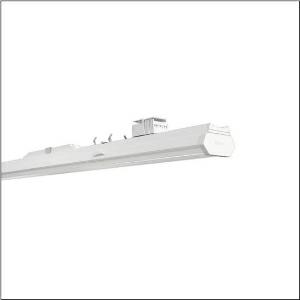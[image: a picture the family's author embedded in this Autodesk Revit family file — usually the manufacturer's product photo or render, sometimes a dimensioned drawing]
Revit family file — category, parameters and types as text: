
# Revit family: licross_r__11_protected_mo_51ts12cn475fd_3ab4
name_source: partatom
category: Lighting Fixtures
units: mm (PartAtom-declared; Revit-internal decimal feet)

## family parameters
Cut with Voids When Loaded = No
Host = Face
Light Source = No
Part Type = Normal
Room Calculation Point = No
Round Connector Dimension = Use Diameter
Shared = No

## types (1)
- --- (1 x LED, 3110 lm, 17.7 W, 4000K)
    Apparent Load = 18 VA
    CIE Flux Codes = 54 82 95 97 100
    Color Rendering = 80
    Color Temperature = 4000K
    Default Elevation = 1800 mm
    Description = Licross® 11 Protected MOluminaire insert, length: 1.500mm, width: 90mm, height: 101mm, LED rated luminous flux: 7.680lm, light colour: 840, control gear: ON/OFF Multilumen, CLOi, control gear: ECG Multilumen, with plug, 6-pole, with phase selection, mains connection: 220..240V, AC/DC, 0/50..60Hz, without changeover relay, for emergency light function, for central battery installations according to DIN EN 60598-2-22, halogen-free wiring, primary optical cover: cover, of PMMA, light emission: direct with ceiling illumination distribution, protection rating (complete): IP50, insulation class (complete): insulation class I (protective earthing), certification: CE, ENEC, VDE, protection symbol: D if used in an environment without relevant dust loads with corresponding accessories, permissible ambient temperature for indoor applications: -35..+40°C, standard: EN 60598-2-22, reducing of maximum allowable ambient temperature of 5°C with ceiling mounting, corresponds to IFS (International Featured Standards) requirements for safety and quality in the food industry, packaging unit: 1 piece
    Height = 92 mm
    Lamp = 1 x LED
    Lamp Light Flux = 3110 lm
    Lamp Power = 17.7 W
    Lamp count = 1
    Length = 1500 mm
    Luminous efficacy = 176 lm/W
    Manufacturer = Siteco
    ModVariant = No
    Model = 51TS12CN475FD
    Mounting Place = Ceiling
    Mounting Type = Pendant
    Number of Poles = 1
    OnlyDefault = Yes
    Power Factor = 1
    Product Name = Licross® 11 Protected MO
    Product group = luminaire insert
    ProductGroupID = 902
    Protection Class = Protection class I
    Protection Degree = IP 50
    RLX_Detail_Level = 1
    RlxData = <blob elided: 22261 chars, md5=3531ed70>
    Socket = socket
    Standby Power = 0 W
    System Light Flux = 3110 lm
    System Power = 18 W
    Type Comments = : DC mode (central or group accumulator) initial emergency light level
    Type Image = l_1256145.jpg
    URL = http://relux.com
    VarID = @adj_134827
    Voltage = 0 V
    Weight = 0.00 kg
    Width = 88 mm

## geometry (parser evidence)
native form markers: Blend x4, Sweep x10
no freeform markers — native parametric forms only
